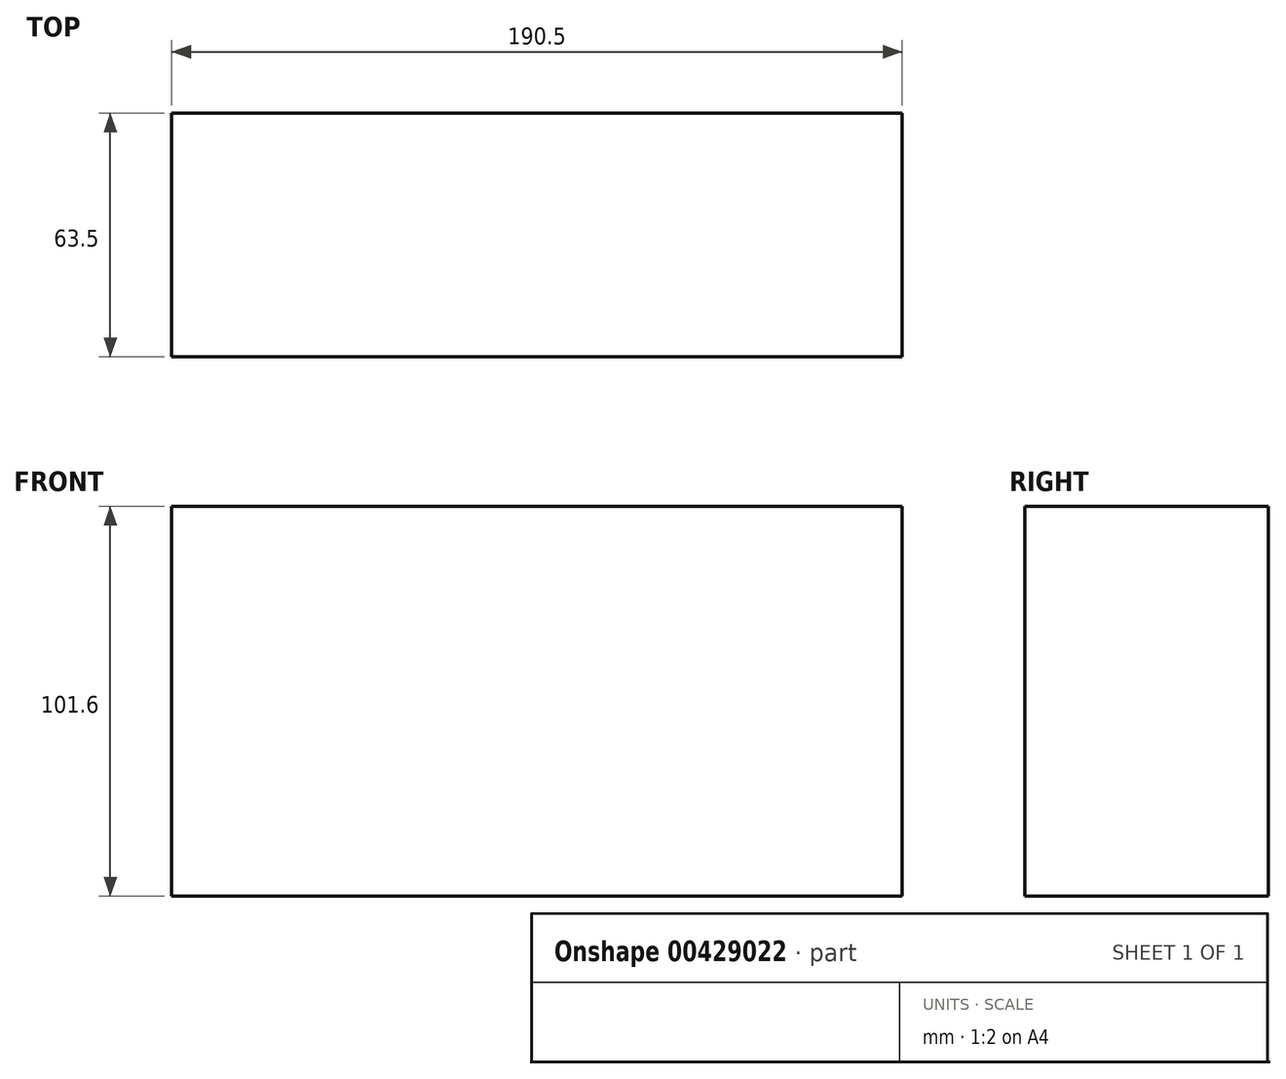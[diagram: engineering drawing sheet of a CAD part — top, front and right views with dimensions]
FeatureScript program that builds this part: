
annotation { "Feature Type Name" : "Feature", "Feature Type Description" : "" }
export const myFeature = defineFeature(function(context is Context, id is Id, definition is map)
    precondition{}
    {
        {
            var Q0;
            Q0=qCreatedBy(makeId("Front.planeOp"),FACE);
            var sketch = newSketch(context, id + "F0", { "sketchPlane" : qUnion([Q0])});
            skLineSegment(sketch, "E0.bottom", {"start": v(-94.9, 0) * mm, "end": v(95.6, 0) * mm});
            skLineSegment(sketch, "E0.top", {"start": v(-94.9, 101.6) * mm, "end": v(95.6, 101.6) * mm});
            skLineSegment(sketch, "E0.left", {"start": v(-94.9, 0) * mm, "end": v(-94.9, 101.6) * mm});
            skLineSegment(sketch, "E0.right", {"start": v(95.6, 0) * mm, "end": v(95.6, 101.6) * mm});
            skSolve(sketch);
        }
        {
            var Q0;
            Q0=makeQuery(id+"F0.imprint","IMPRINT",FACE,{"disambiguationData":[TD([[makeQuery(id+"F0.imprint","IMPRINT",EDGE,{"derivedFrom":sQuery(id+"F0.wireOp",EDGE,"E0.bottom")}),1.0]])]});
            extrude(context, id + "F1", {"entities" : qUnion([Q0]), "depth" : 63.5 * mm});
        }
    });
